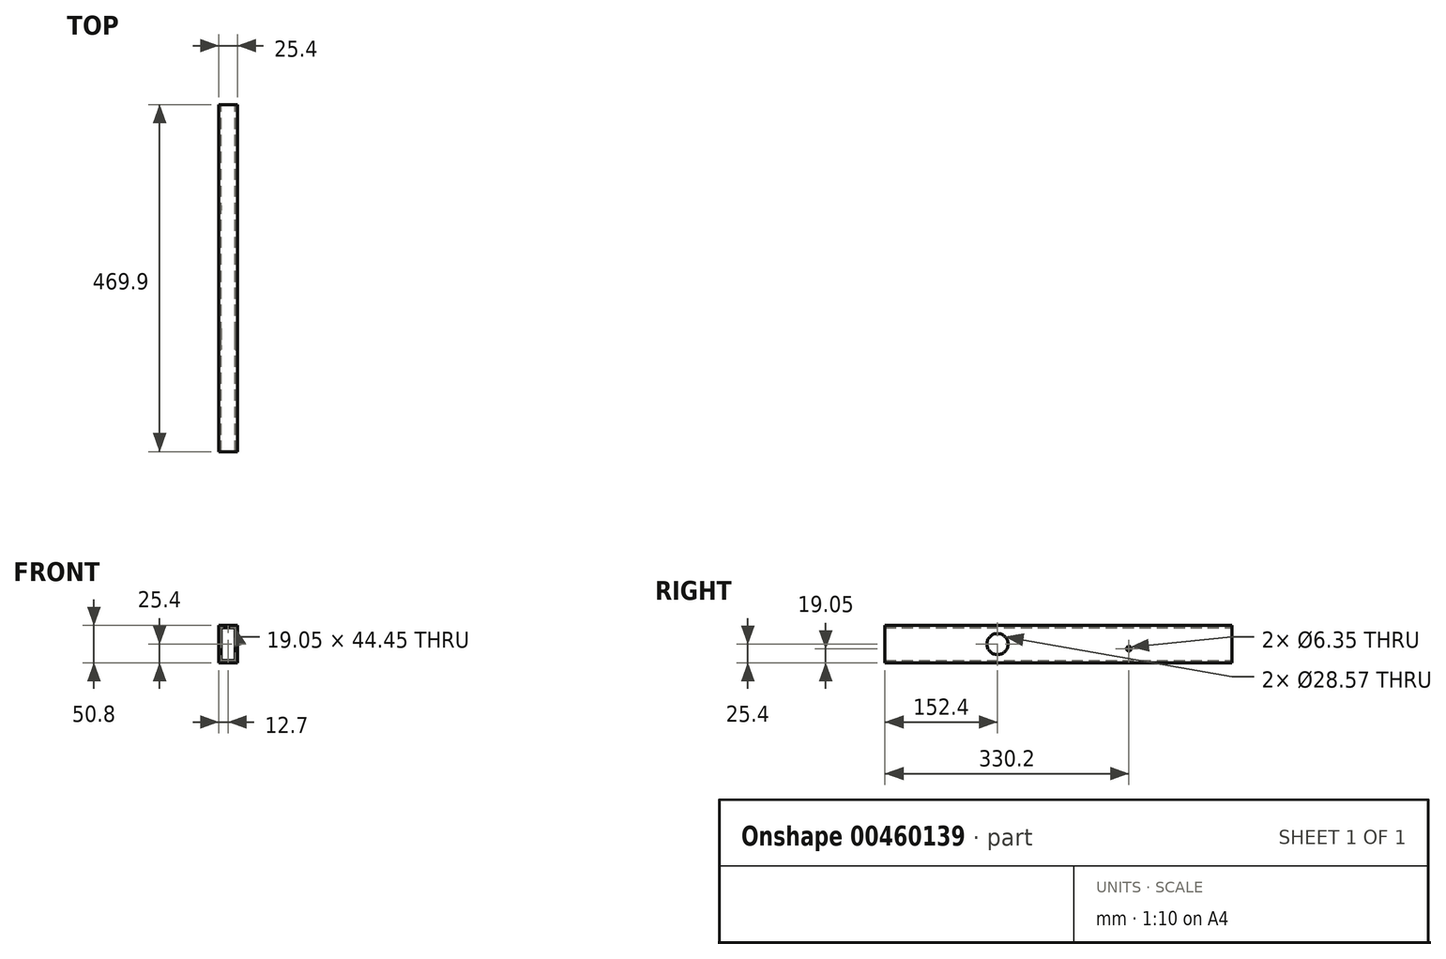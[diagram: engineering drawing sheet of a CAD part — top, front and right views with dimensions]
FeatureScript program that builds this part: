
annotation { "Feature Type Name" : "Feature", "Feature Type Description" : "" }
export const myFeature = defineFeature(function(context is Context, id is Id, definition is map)
    precondition{}
    {
        {
            var Q0;
            Q0=qCreatedBy(makeId("Front.planeOp"),FACE);
            var sketch = newSketch(context, id + "F0", { "sketchPlane" : qUnion([Q0])});
            skLineSegment(sketch, "E0.bottom", {"start": v(12.7, 25.4) * mm, "end": v(-12.7, 25.4) * mm});
            skLineSegment(sketch, "E0.top", {"start": v(12.7, -25.4) * mm, "end": v(-12.7, -25.4) * mm});
            skLineSegment(sketch, "E0.left", {"start": v(12.7, 25.4) * mm, "end": v(12.7, -25.4) * mm});
            skLineSegment(sketch, "E0.right", {"start": v(-12.7, 25.4) * mm, "end": v(-12.7, -25.4) * mm});
            skPoint(sketch, "E0.middle", {"position": v(0, 0) * mm});
            skLineSegment(sketch, "E1.bottom", {"start": v(9.53, 22.23) * mm, "end": v(-9.52, 22.23) * mm});
            skLineSegment(sketch, "E1.top", {"start": v(9.53, -22.23) * mm, "end": v(-9.52, -22.23) * mm});
            skLineSegment(sketch, "E1.left", {"start": v(9.53, 22.23) * mm, "end": v(9.53, -22.23) * mm});
            skLineSegment(sketch, "E1.right", {"start": v(-9.52, 22.23) * mm, "end": v(-9.52, -22.23) * mm});
            skSolve(sketch);
        }
        {
            var Q0;
            Q0=makeQuery(id+"F0.imprint","IMPRINT",FACE,{"disambiguationData":[TD([[makeQuery(id+"F0.imprint","IMPRINT",EDGE,{"derivedFrom":sQuery(id+"F0.wireOp",EDGE,"E0.bottom")}),1.0]])]});
            extrude(context, id + "F1", {"entities" : qUnion([Q0]), "depth" : 469.9 * mm});
        }
        {
            var Q0;
            Q0=makeQuery(id+"F1.opExtrude","SWEPT_FACE",FACE,{"disambiguationData":[OSD([sQuery(id+"F0.wireOp",EDGE,"E0.left")])]});
            var sketch = newSketch(context, id + "F2", { "sketchPlane" : qUnion([Q0])});
            skCircle(sketch, "E2", {"center": v(-317.5, 0) * mm, "radius": 14.29 * mm});
            skCircle(sketch, "E3", {"center": v(-139.7, -6.35) * mm, "radius": 3.18 * mm});
            skLineSegment(sketch, "E4", {"start": v(-317.5, 0) * mm, "end": v(-317.5, 95.43) * mm, "construction": true});
            skSolve(sketch);
        }
        {
            var Q0;
            Q0=makeQuery(id+"F2.imprint","IMPRINT",FACE,{"disambiguationData":[TD([[makeQuery(id+"F2.imprint","IMPRINT",EDGE,{"derivedFrom":sQuery(id+"F2.wireOp",EDGE,"E2")}),1.0]])]});
            var Q1;
            Q1=makeQuery(id+"F2.imprint","IMPRINT",FACE,{"disambiguationData":[TD([[makeQuery(id+"F2.imprint","IMPRINT",EDGE,{"derivedFrom":sQuery(id+"F2.wireOp",EDGE,"E3")}),1.0]])]});
            extrude(context, id + "F3", {"entities" : qUnion([Q0, Q1]), "operationType" : NewBodyOperationType.REMOVE, "oppositeDirection" : true, "depth" : 25.4 * mm});
        }
    });
